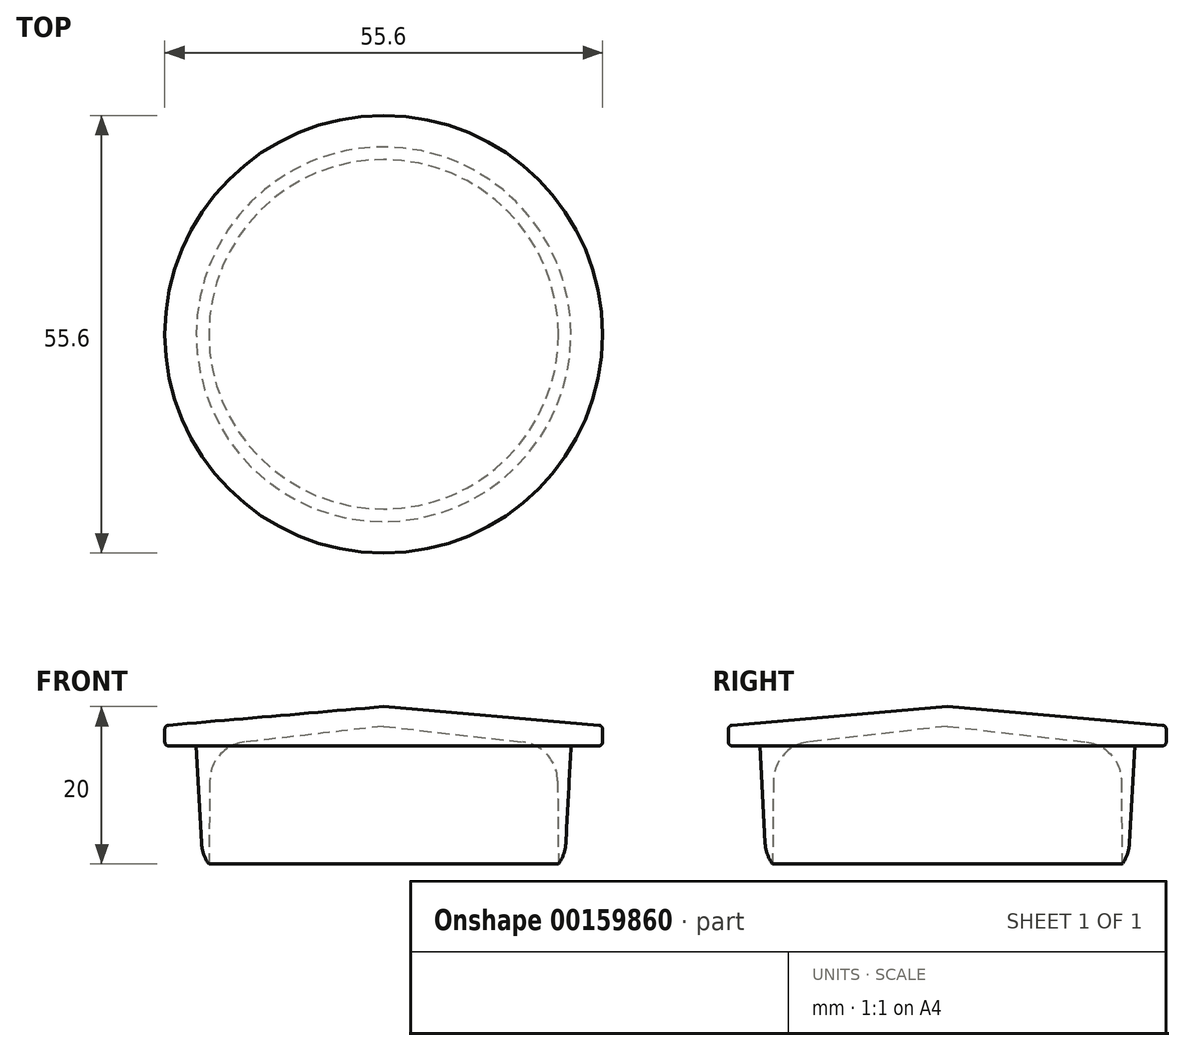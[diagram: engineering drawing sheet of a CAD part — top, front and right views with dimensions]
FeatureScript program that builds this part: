
annotation { "Feature Type Name" : "Feature", "Feature Type Description" : "" }
export const myFeature = defineFeature(function(context is Context, id is Id, definition is map)
    precondition{}
    {
        {
            var Q0;
            Q0=qCreatedBy(makeId("Front.planeOp"),FACE);
            var sketch = newSketch(context, id + "F0", { "sketchPlane" : qUnion([Q0])});
            skLineSegment(sketch, "E0", {"start": v(0, 0) * mm, "end": v(23.8, 0) * mm, "construction": true});
            skLineSegment(sketch, "E1", {"start": v(0, 0) * mm, "end": v(0, -15) * mm, "construction": true});
            skLineSegment(sketch, "E2", {"start": v(0, -15) * mm, "end": v(23, -15) * mm, "construction": true});
            skLineSegment(sketch, "E3", {"start": v(23.8, 0) * mm, "end": v(22.05, 0) * mm});
            skLineSegment(sketch, "E4", {"start": v(23, -15) * mm, "end": v(22.2, -15) * mm});
            skLineSegment(sketch, "E5", {"start": v(22.2, -15) * mm, "end": v(22.05, 0) * mm});
            skLineSegment(sketch, "E6", {"start": v(23.8, 0) * mm, "end": v(23, -15) * mm});
            skLineSegment(sketch, "E7", {"start": v(23.8, 0) * mm, "end": v(27.8, 0) * mm});
            skLineSegment(sketch, "E8", {"start": v(27.8, 0) * mm, "end": v(27.8, 2.6) * mm});
            skLineSegment(sketch, "E9", {"start": v(0, 0) * mm, "end": v(0, 5) * mm, "construction": true});
            skLineSegment(sketch, "E10", {"start": v(0, 5) * mm, "end": v(27.8, 2.6) * mm});
            skLineSegment(sketch, "E11", {"start": v(0, 5) * mm, "end": v(0, 2.5) * mm});
            skLineSegment(sketch, "E12", {"start": v(0, 2.5) * mm, "end": v(22.05, 0) * mm});
            skSolve(sketch);
        }
        {
            var Q0;
            Q0 = qSketchRegion(id + "F0", true);
            var Q1;
            Q1=sQuery(id+"F0.wireOp",EDGE,"E11");
            revolve(context, id + "F1", {"entities" : qUnion([Q0]), "axis" : qUnion([Q1]), "revolveType" : RevolveType.FULL});
        }
        {
            var Q0;
            Q0=makeQuery(id+"F1.opRevolve","SWEPT_EDGE",EDGE,{"disambiguationData":[OSD([sQuery(id+"F0.wireOp",EDGE,"E8"),sQuery(id+"F0.wireOp",EDGE,"E10")])]});
            var Q1;
            Q1=makeQuery(id+"F1.opRevolve","SWEPT_EDGE",EDGE,{"disambiguationData":[OSD([sQuery(id+"F0.wireOp",EDGE,"E7"),sQuery(id+"F0.wireOp",EDGE,"E8")])]});
            fillet(context, id + "F2", {"entities" : qUnion([Q0, Q1]), "radius" : 0.5 * mm, "tangentPropagation" : true, "allowEdgeOverflow" : false});
        }
        {
            var Q0;
            Q0=makeQuery(id+"F1.opRevolve","SWEPT_EDGE",EDGE,{"disambiguationData":[OSD([sQuery(id+"F0.wireOp",EDGE,"E4"),sQuery(id+"F0.wireOp",EDGE,"E6")])]});
            var Q1;
            Q1=makeQuery(id+"F1.opRevolve","SWEPT_EDGE",EDGE,{"disambiguationData":[OSD([sQuery(id+"F0.wireOp",EDGE,"E3"),sQuery(id+"F0.wireOp",EDGE,"E5"),sQuery(id+"F0.wireOp",EDGE,"E12")])]});
            fillet(context, id + "F3", {"entities" : qUnion([Q0, Q1]), "radius" : 5 * mm, "tangentPropagation" : true, "allowEdgeOverflow" : false});
        }
    });
